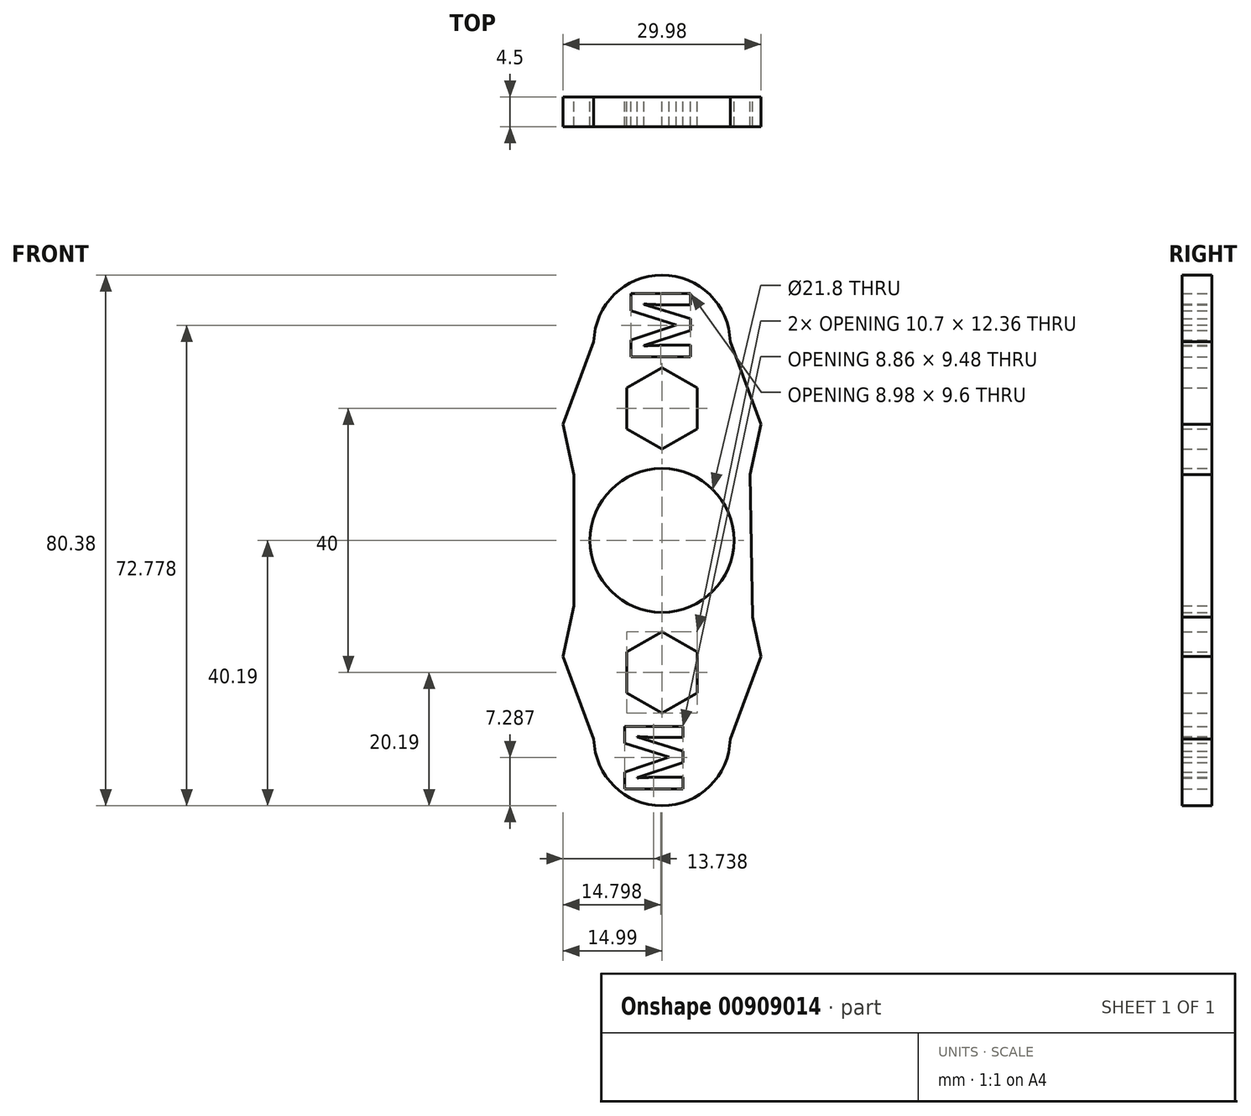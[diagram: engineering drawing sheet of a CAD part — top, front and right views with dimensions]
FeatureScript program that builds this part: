
annotation { "Feature Type Name" : "Feature", "Feature Type Description" : "" }
export const myFeature = defineFeature(function(context is Context, id is Id, definition is map)
    precondition{}
    {
        {
            var Q0;
            Q0=qCreatedBy(makeId("Front.planeOp"),FACE);
            var sketch = newSketch(context, id + "F0", { "sketchPlane" : qUnion([Q0])});
            skCircle(sketch, "E0", {"center": v(0, 0) * mm, "radius": 10.9 * mm});
            skLineSegment(sketch, "E1", {"start": v(0, 13.82) * mm, "end": v(0, 14.65) * mm});
            skArc(sketch, "E2", {"start": v(-10.32, -30.08) * mm, "mid": v(0.1, -40.2) * mm, "end": v(10.33, -29.87) * mm});
            skLineSegment(sketch, "E3", {"start": v(-10.32, -30.08) * mm, "end": v(-14.99, -17.58) * mm});
            skLineSegment(sketch, "E4", {"start": v(-14.99, -17.58) * mm, "end": v(-13.31, -9.89) * mm});
            skLineSegment(sketch, "E5.MirrorCS", {"start": v(10.32, -30.08) * mm, "end": v(14.99, -17.58) * mm});
            skLineSegment(sketch, "E6.MirrorCS", {"start": v(14.99, -17.58) * mm, "end": v(13.7, -11.65) * mm});
            skLineSegment(sketch, "E7.MirrorCS", {"start": v(-14.99, 17.58) * mm, "end": v(-13.31, 9.89) * mm});
            skLineSegment(sketch, "E8.MirrorCS", {"start": v(10.32, 30.08) * mm, "end": v(14.99, 17.58) * mm});
            skArc(sketch, "E9.MirrorCS", {"start": v(-10.32, 30.08) * mm, "mid": v(0.1, 40.2) * mm, "end": v(10.33, 29.87) * mm});
            skLineSegment(sketch, "E10.MirrorCS", {"start": v(-10.32, 30.08) * mm, "end": v(-14.99, 17.58) * mm});
            skLineSegment(sketch, "E11.MirrorCS", {"start": v(14.99, 17.58) * mm, "end": v(13.33, 9.99) * mm});
            skArc(sketch, "E12.MirrorCS", {"start": v(10.32, 30.08) * mm, "mid": v(-0.1, 40.2) * mm, "end": v(-10.33, 29.87) * mm});
            skCircle(sketch, "E13.cCircle", {"center": v(0, -20) * mm, "radius": 5.35 * mm, "construction": true});
            skLineSegment(sketch, "E13.0", {"start": v(-5.35, -23.09) * mm, "end": v(-5.35, -16.91) * mm});
            skLineSegment(sketch, "E13.1", {"start": v(-5.35, -16.91) * mm, "end": v(0, -13.82) * mm});
            skLineSegment(sketch, "E13.2", {"start": v(0, -13.82) * mm, "end": v(5.35, -16.91) * mm});
            skLineSegment(sketch, "E13.3", {"start": v(5.35, -16.91) * mm, "end": v(5.35, -23.09) * mm});
            skLineSegment(sketch, "E13.4", {"start": v(5.35, -23.09) * mm, "end": v(0, -26.18) * mm});
            skLineSegment(sketch, "E13.5", {"start": v(0, -26.18) * mm, "end": v(-5.35, -23.09) * mm});
            skPoint(sketch, "E13.0.midPoint", {"position": v(-5.35, -20) * mm});
            skLineSegment(sketch, "E14.MirrorCS", {"start": v(5.35, 23.09) * mm, "end": v(0, 26.18) * mm});
            skPoint(sketch, "E15.MirrorP", {"position": v(-5.35, 20) * mm});
            skLineSegment(sketch, "E16.MirrorCS", {"start": v(0, 26.18) * mm, "end": v(-5.35, 23.09) * mm});
            skCircle(sketch, "E17.MirrorC", {"center": v(0, 20) * mm, "radius": 5.35 * mm, "construction": true});
            skLineSegment(sketch, "E18.MirrorCS", {"start": v(-5.35, 16.91) * mm, "end": v(0, 13.82) * mm});
            skLineSegment(sketch, "E19.MirrorCS", {"start": v(5.35, 16.91) * mm, "end": v(5.35, 23.09) * mm});
            skLineSegment(sketch, "E20.MirrorCS", {"start": v(0, 13.82) * mm, "end": v(5.35, 16.91) * mm});
            skLineSegment(sketch, "E21.MirrorCS", {"start": v(-5.35, 23.09) * mm, "end": v(-5.35, 16.91) * mm});
            skLineSegment(sketch, "E22.trimOffspring", {"start": v(0, 25.35) * mm, "end": v(0, 26.18) * mm});
            skPoint(sketch, "E23.MirrorCS.start.orphan", {"position": v(14.99, 17.58) * mm});
            skLineSegment(sketch, "E24", {"start": v(13.33, 9.99) * mm, "end": v(13.7, -11.65) * mm});
            skPoint(sketch, "E24.endSnap0", {"position": v(13.7, 11.65) * mm});
            skLineSegment(sketch, "E25", {"start": v(-13.31, 9.89) * mm, "end": v(-13.31, -9.89) * mm});
            skSolve(sketch);
        }
        {
            var Q0;
            Q0=qSketchRegion(id+"F0",true);
            extrude(context, id + "F1", {"entities" : qUnion([Q0]), "depth" : 4.5 * mm, "offsetDistance" : 25 * mm});
        }
        {
            var Q0;
            Q0=makeQuery(id+"F1.opExtrude","CAP_FACE",FACE,{"disambiguationData":[OSD([sQuery(id+"F0.wireOp",EDGE,"E0"),sQuery(id+"F0.wireOp",EDGE,"E5.MirrorCS"),sQuery(id+"F0.wireOp",EDGE,"E6.MirrorCS"),sQuery(id+"F0.wireOp",EDGE,"E8.MirrorCS"),sQuery(id+"F0.wireOp",EDGE,"E11.MirrorCS"),sQuery(id+"F0.wireOp",EDGE,"E2"),sQuery(id+"F0.wireOp",EDGE,"E3"),sQuery(id+"F0.wireOp",EDGE,"E12.MirrorCS"),sQuery(id+"F0.wireOp",EDGE,"E10.MirrorCS"),sQuery(id+"F0.wireOp",EDGE,"E7.MirrorCS"),sQuery(id+"F0.wireOp",EDGE,"E4"),sQuery(id+"F0.wireOp",EDGE,"E13.0"),sQuery(id+"F0.wireOp",EDGE,"E13.1"),sQuery(id+"F0.wireOp",EDGE,"E13.2"),sQuery(id+"F0.wireOp",EDGE,"E13.3"),sQuery(id+"F0.wireOp",EDGE,"E13.4"),sQuery(id+"F0.wireOp",EDGE,"E13.5"),sQuery(id+"F0.wireOp",EDGE,"E14.MirrorCS"),sQuery(id+"F0.wireOp",EDGE,"E16.MirrorCS"),sQuery(id+"F0.wireOp",EDGE,"E18.MirrorCS"),sQuery(id+"F0.wireOp",EDGE,"E19.MirrorCS"),sQuery(id+"F0.wireOp",EDGE,"E20.MirrorCS"),sQuery(id+"F0.wireOp",EDGE,"E21.MirrorCS"),sQuery(id+"F0.wireOp",EDGE,"E24"),sQuery(id+"F0.wireOp",EDGE,"E25")])],"isStart":true});
            var sketch = newSketch(context, id + "F2", { "sketchPlane" : qUnion([Q0])});
            skText(sketch, "E26", { "text": "M", "fontName": "OpenSans-Bold.ttf"});
            skText(sketch, "E27", { "text": "M", "fontName": "OpenSans-Bold.ttf"});
            skText(sketch, "E28", { "text": "M", "fontName": "OpenSans-Bold.ttf"});
            const initialGuessF2  = {"E26": [-0.0236, -0.06557, 1, 0, 0.00906], "E27": [-0.0043, 0.03852, 0, -1, 0.00906], "E28": [-0.00318, -0.02705, 0, -1, 0.00894]};
            skSetInitialGuess(sketch, initialGuessF2);
            skSolve(sketch);
        }
        {
            var Q0;
            Q0=qSketchRegion(id+"F2",true);
            var Q1;
            Q1=qConstructionFilter(qBodyType(qCreatedBy(id+"F2",EDGE),BodyType.WIRE),ConstructionObject.NO);
            extrude(context, id + "F3", {"entities" : qUnion([Q0]), "operationType" : NewBodyOperationType.REMOVE, "surfaceEntities" : qUnion([Q1]), "oppositeDirection" : true, "depth" : 25 * mm, "offsetDistance" : 25 * mm});
        }
    });
